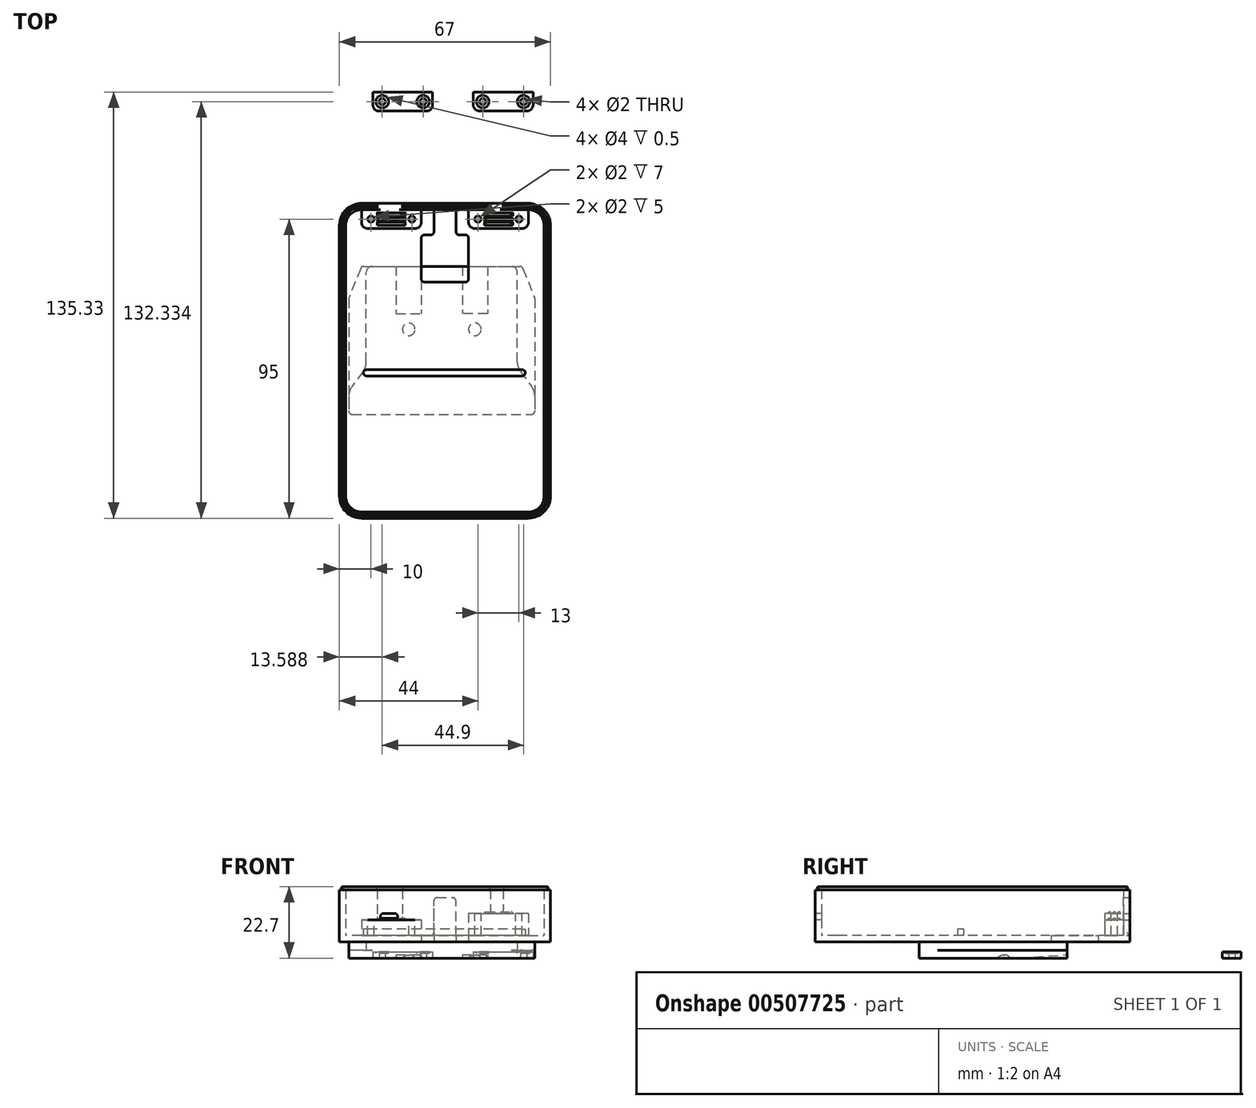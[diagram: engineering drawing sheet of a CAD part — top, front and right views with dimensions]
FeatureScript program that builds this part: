
annotation { "Feature Type Name" : "Feature", "Feature Type Description" : "" }
export const myFeature = defineFeature(function(context is Context, id is Id, definition is map)
    precondition{}
    {
        {
            var Q0;
            Q0=qCreatedBy(makeId("Top.planeOp"),FACE);
            var sketch = newSketch(context, id + "F0", { "sketchPlane" : qUnion([Q0])});
            skLineSegment(sketch, "E0.bottom", {"start": v(4, 0) * mm, "end": v(55, 0) * mm});
            skLineSegment(sketch, "E0.top", {"start": v(0, -47) * mm, "end": v(59, -47) * mm});
            skLineSegment(sketch, "E0.left", {"start": v(0, -10) * mm, "end": v(0, -47) * mm});
            skLineSegment(sketch, "E0.right", {"start": v(59, -10) * mm, "end": v(59, -47) * mm});
            skLineSegment(sketch, "E1", {"start": v(4, 0) * mm, "end": v(0, -10) * mm});
            skPoint(sketch, "E2.orphan", {"position": v(0, 0) * mm});
            skLineSegment(sketch, "E3", {"start": v(55, 0) * mm, "end": v(59, -10) * mm});
            skPoint(sketch, "E4.orphan", {"position": v(59, 0) * mm});
            skSolve(sketch);
        }
        {
            var Q0;
            Q0=makeQuery(id+"F0.imprint","IMPRINT",FACE,{"disambiguationData":[TD([[makeQuery(id+"F0.imprint","IMPRINT",EDGE,{"derivedFrom":sQuery(id+"F0.wireOp",EDGE,"E0.bottom")}),-1.0]])]});
            extrude(context, id + "F1", {"entities" : qUnion([Q0]), "depth" : 2.5 * mm, "offsetDistance" : 25 * mm});
        }
        {
            var Q0;
            Q0=makeQuery(id+"F1.opExtrude","CAP_FACE",FACE,{"disambiguationData":[OSD([sQuery(id+"F0.wireOp",EDGE,"E0.bottom"),sQuery(id+"F0.wireOp",EDGE,"E0.top"),sQuery(id+"F0.wireOp",EDGE,"E0.left"),sQuery(id+"F0.wireOp",EDGE,"E0.right"),sQuery(id+"F0.wireOp",EDGE,"E1"),sQuery(id+"F0.wireOp",EDGE,"E3")])],"isStart":false});
            var sketch = newSketch(context, id + "F2", { "sketchPlane" : qUnion([Q0])});
            skLineSegment(sketch, "E5.bottom", {"start": v(0, -47) * mm, "end": v(59, -47) * mm});
            skLineSegment(sketch, "E5.left", {"start": v(0, -47) * mm, "end": v(0, -39.5) * mm});
            skLineSegment(sketch, "E5.right", {"start": v(59, -47) * mm, "end": v(59, -39.5) * mm});
            skLineSegment(sketch, "E6.top", {"start": v(7.5, 0) * mm, "end": v(51.5, 0) * mm});
            skLineSegment(sketch, "E6.left", {"start": v(5.5, -32) * mm, "end": v(5.5, -2) * mm});
            skLineSegment(sketch, "E6.right", {"start": v(53.5, -32) * mm, "end": v(53.5, -2) * mm});
            skPoint(sketch, "E7.visualSharp", {"position": v(5.5, 0) * mm});
            skArc(sketch, "E7.filletArc", {"start": v(7.5, 0) * mm, "mid": v(6.09, -0.59) * mm, "end": v(5.5, -2) * mm});
            skPoint(sketch, "E8.visualSharp", {"position": v(53.5, 0) * mm});
            skArc(sketch, "E8.filletArc", {"start": v(53.5, -2) * mm, "mid": v(52.91, -0.59) * mm, "end": v(51.5, 0) * mm});
            skLineSegment(sketch, "E9", {"start": v(53.5, -32) * mm, "end": v(59, -39.5) * mm});
            skLineSegment(sketch, "E10", {"start": v(5.5, -32) * mm, "end": v(0, -39.5) * mm});
            skPoint(sketch, "E11.orphan", {"position": v(0, -32) * mm});
            skPoint(sketch, "E12.orphan", {"position": v(59, -32) * mm});
            skSolve(sketch);
        }
        {
            var Q0;
            Q0=makeQuery(id+"F2.imprint","IMPRINT",FACE,{"disambiguationData":[TD([[makeQuery(id+"F2.imprint","IMPRINT",EDGE,{"derivedFrom":sQuery(id+"F2.wireOp",EDGE,"E5.bottom")}),1.0]])]});
            extrude(context, id + "F3", {"entities" : qUnion([Q0]), "operationType" : NewBodyOperationType.ADD, "depth" : 2.7 * mm, "offsetDistance" : 25 * mm});
        }
        {
            var Q0;
            Q0=makeQuery(id+"F3.opExtrude","CAP_FACE",FACE,{"disambiguationData":[OSD([sQuery(id+"F2.wireOp",EDGE,"E5.bottom"),sQuery(id+"F2.wireOp",EDGE,"E5.left"),sQuery(id+"F2.wireOp",EDGE,"E5.right"),sQuery(id+"F2.wireOp",EDGE,"E6.top"),sQuery(id+"F2.wireOp",EDGE,"E6.left"),sQuery(id+"F2.wireOp",EDGE,"E6.right"),sQuery(id+"F2.wireOp",EDGE,"E7.filletArc"),sQuery(id+"F2.wireOp",EDGE,"E8.filletArc"),sQuery(id+"F2.wireOp",EDGE,"E9"),sQuery(id+"F2.wireOp",EDGE,"E10")])],"isStart":false});
            var sketch = newSketch(context, id + "F4", { "sketchPlane" : qUnion([Q0])});
            skLineSegment(sketch, "E13.bottom", {"start": v(57, -80) * mm, "end": v(4, -80) * mm});
            skLineSegment(sketch, "E13.top", {"start": v(57, 20) * mm, "end": v(35, 20) * mm});
            skLineSegment(sketch, "E13.left", {"start": v(64, -73) * mm, "end": v(64, 13) * mm});
            skLineSegment(sketch, "E13.right", {"start": v(-3, -73) * mm, "end": v(-3, 13) * mm});
            skPoint(sketch, "E14.visualSharp", {"position": v(-3, 20) * mm});
            skArc(sketch, "E14.filletArc", {"start": v(4, 20) * mm, "mid": v(-0.95, 17.95) * mm, "end": v(-3, 13) * mm});
            skPoint(sketch, "E15.visualSharp", {"position": v(64, 20) * mm});
            skArc(sketch, "E15.filletArc", {"start": v(64, 13) * mm, "mid": v(61.95, 17.95) * mm, "end": v(57, 20) * mm});
            skPoint(sketch, "E16.visualSharp", {"position": v(64, -80) * mm});
            skArc(sketch, "E16.filletArc", {"start": v(57, -80) * mm, "mid": v(61.95, -77.95) * mm, "end": v(64, -73) * mm});
            skPoint(sketch, "E17.visualSharp", {"position": v(-3, -80) * mm});
            skArc(sketch, "E17.filletArc", {"start": v(-3, -73) * mm, "mid": v(-0.95, -77.95) * mm, "end": v(4, -80) * mm});
            skLineSegment(sketch, "E18.top", {"start": v(27, -5) * mm, "end": v(34, -5) * mm});
            skLineSegment(sketch, "E18.left", {"start": v(27, 19) * mm, "end": v(27, 11) * mm});
            skLineSegment(sketch, "E18.right", {"start": v(34, 19) * mm, "end": v(34, 11) * mm});
            skLineSegment(sketch, "E19.filletArc", {"start": v(27, -5) * mm, "end": v(27, -5) * mm});
            skLineSegment(sketch, "E20.filletArc", {"start": v(34, -5) * mm, "end": v(34, -5) * mm});
            skLineSegment(sketch, "E21.trimOffspring", {"start": v(26, 20) * mm, "end": v(4, 20) * mm});
            skPoint(sketch, "E22.visualSharp", {"position": v(27, 20) * mm});
            skArc(sketch, "E22.filletArc", {"start": v(27, 19) * mm, "mid": v(26.7, 19.7) * mm, "end": v(26, 20) * mm});
            skPoint(sketch, "E23.visualSharp", {"position": v(34, 20) * mm});
            skArc(sketch, "E23.filletArc", {"start": v(35, 20) * mm, "mid": v(34.3, 19.7) * mm, "end": v(34, 19) * mm});
            skPoint(sketch, "E24", {"position": v(34, 10) * mm});
            skLineSegment(sketch, "E25", {"start": v(34, -5) * mm, "end": v(37, -5) * mm});
            skLineSegment(sketch, "E26", {"start": v(38, -4) * mm, "end": v(38, 9) * mm});
            skLineSegment(sketch, "E27", {"start": v(37, 10) * mm, "end": v(35, 10) * mm});
            skPoint(sketch, "E28", {"position": v(27, 10) * mm});
            skLineSegment(sketch, "E29", {"start": v(26, 10) * mm, "end": v(24, 10) * mm});
            skLineSegment(sketch, "E30", {"start": v(23, 9) * mm, "end": v(23, -4) * mm});
            skLineSegment(sketch, "E31", {"start": v(24, -5) * mm, "end": v(27, -5) * mm});
            skPoint(sketch, "E32.visualSharp", {"position": v(23, 10) * mm});
            skArc(sketch, "E32.filletArc", {"start": v(24, 10) * mm, "mid": v(23.3, 9.7) * mm, "end": v(23, 9) * mm});
            skPoint(sketch, "E33.visualSharp", {"position": v(23, -5) * mm});
            skArc(sketch, "E33.filletArc", {"start": v(23, -4) * mm, "mid": v(23.3, -4.7) * mm, "end": v(24, -5) * mm});
            skPoint(sketch, "E34.visualSharp", {"position": v(38, -5) * mm});
            skArc(sketch, "E34.filletArc", {"start": v(37, -5) * mm, "mid": v(37.7, -4.7) * mm, "end": v(38, -4) * mm});
            skPoint(sketch, "E35.visualSharp", {"position": v(38, 10) * mm});
            skArc(sketch, "E35.filletArc", {"start": v(38, 9) * mm, "mid": v(37.7, 9.7) * mm, "end": v(37, 10) * mm});
            skArc(sketch, "E36.filletArc", {"start": v(26, 10) * mm, "mid": v(26.7, 10.3) * mm, "end": v(27, 11) * mm});
            skArc(sketch, "E37.filletArc", {"start": v(34, 11) * mm, "mid": v(34.3, 10.3) * mm, "end": v(35, 10) * mm});
            skSolve(sketch);
        }
        {
            var Q0;
            Q0 = qSketchRegion(id + "F4", true);
            extrude(context, id + "F5", {"entities" : qUnion([Q0]), "operationType" : NewBodyOperationType.ADD, "depth" : 2 * mm, "offsetDistance" : 25 * mm});
        }
        {
            var Q0;
            Q0=makeQuery(id+"F5.opExtrude","CAP_FACE",FACE,{"disambiguationData":[OSD([sQuery(id+"F4.wireOp",EDGE,"E13.bottom"),sQuery(id+"F4.wireOp",EDGE,"E13.top"),sQuery(id+"F4.wireOp",EDGE,"E13.left"),sQuery(id+"F4.wireOp",EDGE,"E13.right"),sQuery(id+"F4.wireOp",EDGE,"E14.filletArc"),sQuery(id+"F4.wireOp",EDGE,"E15.filletArc"),sQuery(id+"F4.wireOp",EDGE,"E16.filletArc"),sQuery(id+"F4.wireOp",EDGE,"E17.filletArc"),sQuery(id+"F4.wireOp",EDGE,"E18.top"),sQuery(id+"F4.wireOp",EDGE,"E18.left"),sQuery(id+"F4.wireOp",EDGE,"E18.right"),sQuery(id+"F4.wireOp",EDGE,"E19.filletArc"),sQuery(id+"F4.wireOp",EDGE,"E20.filletArc"),sQuery(id+"F4.wireOp",EDGE,"E21.trimOffspring"),sQuery(id+"F4.wireOp",EDGE,"E22.filletArc"),sQuery(id+"F4.wireOp",EDGE,"E23.filletArc")])],"isStart":false});
            var sketch = newSketch(context, id + "F6", { "sketchPlane" : qUnion([Q0])});
            skLineSegment(sketch, "E38.bottom", {"start": v(57, 20) * mm, "end": v(4, 20) * mm});
            skLineSegment(sketch, "E38.top", {"start": v(57, -80) * mm, "end": v(4, -80) * mm});
            skLineSegment(sketch, "E38.left", {"start": v(64, 13) * mm, "end": v(64, -73) * mm});
            skLineSegment(sketch, "E38.right", {"start": v(-3, 13) * mm, "end": v(-3, -73) * mm});
            skPoint(sketch, "E39.visualSharp", {"position": v(-3, 20) * mm});
            skArc(sketch, "E39.filletArc", {"start": v(4, 20) * mm, "mid": v(-0.95, 17.95) * mm, "end": v(-3, 13) * mm});
            skPoint(sketch, "E40.visualSharp", {"position": v(64, 20) * mm});
            skArc(sketch, "E40.filletArc", {"start": v(64, 13) * mm, "mid": v(61.95, 17.95) * mm, "end": v(57, 20) * mm});
            skPoint(sketch, "E41.visualSharp", {"position": v(64, -80) * mm});
            skArc(sketch, "E41.filletArc", {"start": v(57, -80) * mm, "mid": v(61.95, -77.95) * mm, "end": v(64, -73) * mm});
            skPoint(sketch, "E42.visualSharp", {"position": v(-3, -80) * mm});
            skArc(sketch, "E42.filletArc", {"start": v(-3, -73) * mm, "mid": v(-0.95, -77.95) * mm, "end": v(4, -80) * mm});
            skArc(sketch, "E43.0", {"start": v(62, 13) * mm, "mid": v(60.54, 16.54) * mm, "end": v(57, 18) * mm});
            skLineSegment(sketch, "E43.1", {"start": v(62, 13) * mm, "end": v(62, -73) * mm});
            skLineSegment(sketch, "E43.2", {"start": v(57, 18) * mm, "end": v(4, 18) * mm});
            skArc(sketch, "E43.3", {"start": v(57, -78) * mm, "mid": v(60.54, -76.54) * mm, "end": v(62, -73) * mm});
            skArc(sketch, "E43.4", {"start": v(4, 18) * mm, "mid": v(0.46, 16.54) * mm, "end": v(-1, 13) * mm});
            skLineSegment(sketch, "E43.5", {"start": v(-1, 13) * mm, "end": v(-1, -73) * mm});
            skArc(sketch, "E43.6", {"start": v(-1, -73) * mm, "mid": v(0.46, -76.54) * mm, "end": v(4, -78) * mm});
            skLineSegment(sketch, "E43.7", {"start": v(57, -78) * mm, "end": v(4, -78) * mm});
            skSolve(sketch);
        }
        {
            var Q0;
            Q0 = qSketchRegion(id + "F6", true);
            extrude(context, id + "F7", {"entities" : qUnion([Q0]), "operationType" : NewBodyOperationType.ADD, "depth" : 14.5 * mm, "offsetDistance" : 25 * mm});
        }
        {
            var Q0;
            Q0=makeQuery(id+"F7.boolean.opBoolean","MERGE",FACE,{"derivedFrom":[makeQuery(id+"F5.opExtrude","SWEPT_FACE",FACE,{"disambiguationData":[OSD([sQuery(id+"F4.wireOp",EDGE,"E13.top")])]}),makeQuery(id+"F5.opExtrude","SWEPT_FACE",FACE,{"disambiguationData":[OSD([sQuery(id+"F4.wireOp",EDGE,"E21.trimOffspring")])]}),makeQuery(id+"F7.opExtrude","SWEPT_FACE",FACE,{"disambiguationData":[OSD([sQuery(id+"F6.wireOp",EDGE,"E38.bottom")])]})]});
            var sketch = newSketch(context, id + "F8", { "sketchPlane" : qUnion([Q0])});
            skLineSegment(sketch, "E44.bottom", {"start": v(-27, 7.2) * mm, "end": v(-34, 7.2) * mm});
            skLineSegment(sketch, "E44.top", {"start": v(-28, 19.2) * mm, "end": v(-33, 19.2) * mm});
            skLineSegment(sketch, "E44.left", {"start": v(-27, 7.2) * mm, "end": v(-27, 18.2) * mm});
            skLineSegment(sketch, "E44.right", {"start": v(-34, 7.2) * mm, "end": v(-34, 18.2) * mm});
            skPoint(sketch, "E45.visualSharp", {"position": v(-34, 19.2) * mm});
            skArc(sketch, "E45.filletArc", {"start": v(-33, 19.2) * mm, "mid": v(-33.7, 18.9) * mm, "end": v(-34, 18.2) * mm});
            skPoint(sketch, "E46.visualSharp", {"position": v(-27, 19.2) * mm});
            skArc(sketch, "E46.filletArc", {"start": v(-27, 18.2) * mm, "mid": v(-27.3, 18.9) * mm, "end": v(-28, 19.2) * mm});
            skLineSegment(sketch, "E47.bottom", {"start": v(-49, 21.7) * mm, "end": v(-45, 21.7) * mm});
            skLineSegment(sketch, "E47.top", {"start": v(-48, 14.2) * mm, "end": v(-46, 14.2) * mm});
            skLineSegment(sketch, "E47.left", {"start": v(-49, 21.7) * mm, "end": v(-49, 15.2) * mm});
            skLineSegment(sketch, "E47.right", {"start": v(-45, 21.7) * mm, "end": v(-45, 15.2) * mm});
            skPoint(sketch, "E48.visualSharp", {"position": v(-49, 14.2) * mm});
            skArc(sketch, "E48.filletArc", {"start": v(-49, 15.2) * mm, "mid": v(-48.7, 14.5) * mm, "end": v(-48, 14.2) * mm});
            skPoint(sketch, "E49.visualSharp", {"position": v(-45, 14.2) * mm});
            skArc(sketch, "E49.filletArc", {"start": v(-46, 14.2) * mm, "mid": v(-45.3, 14.5) * mm, "end": v(-45, 15.2) * mm});
            skLineSegment(sketch, "E50.bottom", {"start": v(-9, 21.7) * mm, "end": v(-17, 21.7) * mm});
            skLineSegment(sketch, "E50.top", {"start": v(-10, 12.2) * mm, "end": v(-16, 12.2) * mm});
            skLineSegment(sketch, "E50.left", {"start": v(-9, 21.7) * mm, "end": v(-9, 13.2) * mm});
            skLineSegment(sketch, "E50.right", {"start": v(-17, 21.7) * mm, "end": v(-17, 13.2) * mm});
            skPoint(sketch, "E51.visualSharp", {"position": v(-17, 12.2) * mm});
            skArc(sketch, "E51.filletArc", {"start": v(-17, 13.2) * mm, "mid": v(-16.7, 12.5) * mm, "end": v(-16, 12.2) * mm});
            skPoint(sketch, "E52.visualSharp", {"position": v(-9, 12.2) * mm});
            skArc(sketch, "E52.filletArc", {"start": v(-10, 12.2) * mm, "mid": v(-9.3, 12.5) * mm, "end": v(-9, 13.2) * mm});
            skSolve(sketch);
        }
        {
            var Q0;
            Q0=makeQuery(id+"FvWDrRj3cYPkLqx_1.boolean.opBoolean","MERGE",FACE,{"derivedFrom":[makeQuery(id+"F5.opExtrude","CAP_FACE",FACE,{"disambiguationData":[OSD([sQuery(id+"F4.wireOp",EDGE,"E13.bottom"),sQuery(id+"F4.wireOp",EDGE,"E13.top"),sQuery(id+"F4.wireOp",EDGE,"E13.left"),sQuery(id+"F4.wireOp",EDGE,"E13.right"),sQuery(id+"F4.wireOp",EDGE,"E14.filletArc"),sQuery(id+"F4.wireOp",EDGE,"E15.filletArc"),sQuery(id+"F4.wireOp",EDGE,"E16.filletArc"),sQuery(id+"F4.wireOp",EDGE,"E17.filletArc"),sQuery(id+"F4.wireOp",EDGE,"E18.top"),sQuery(id+"F4.wireOp",EDGE,"E18.left"),sQuery(id+"F4.wireOp",EDGE,"E18.right"),sQuery(id+"F4.wireOp",EDGE,"E19.filletArc"),sQuery(id+"F4.wireOp",EDGE,"E20.filletArc"),sQuery(id+"F4.wireOp",EDGE,"E21.trimOffspring"),sQuery(id+"F4.wireOp",EDGE,"E22.filletArc"),sQuery(id+"F4.wireOp",EDGE,"E23.filletArc")])],"isStart":false}),makeQuery(id+"FvWDrRj3cYPkLqx_1.opExtrude","SWEPT_FACE",FACE,{"disambiguationData":[OSD([sQuery(id+"F8.wireOp",EDGE,"E44.bottom")])]})]});
            var sketch = newSketch(context, id + "F9", { "sketchPlane" : qUnion([Q0])});
            skLineSegment(sketch, "E53.bottom", {"start": v(54.99, -34.8) * mm, "end": v(5.63, -34.8) * mm});
            skLineSegment(sketch, "E53.top", {"start": v(54.99, -32.8) * mm, "end": v(5.63, -32.8) * mm});
            skLineSegment(sketch, "E53.left", {"start": v(55.99, -33.8) * mm, "end": v(55.99, -33.8) * mm});
            skLineSegment(sketch, "E53.right", {"start": v(4.63, -33.8) * mm, "end": v(4.63, -33.8) * mm});
            skPoint(sketch, "E54.visualSharp", {"position": v(4.63, -32.8) * mm});
            skArc(sketch, "E54.filletArc", {"start": v(5.63, -32.8) * mm, "mid": v(4.92, -33.1) * mm, "end": v(4.63, -33.8) * mm});
            skPoint(sketch, "E55.visualSharp", {"position": v(4.63, -34.8) * mm});
            skArc(sketch, "E55.filletArc", {"start": v(4.63, -33.8) * mm, "mid": v(4.92, -34.5) * mm, "end": v(5.63, -34.8) * mm});
            skPoint(sketch, "E56.visualSharp", {"position": v(55.99, -32.8) * mm});
            skArc(sketch, "E56.filletArc", {"start": v(55.99, -33.8) * mm, "mid": v(55.7, -33.1) * mm, "end": v(54.99, -32.8) * mm});
            skPoint(sketch, "E57.visualSharp", {"position": v(55.99, -34.8) * mm});
            skArc(sketch, "E57.filletArc", {"start": v(54.99, -34.8) * mm, "mid": v(55.7, -34.5) * mm, "end": v(55.99, -33.8) * mm});
            skSolve(sketch);
        }
        {
            var Q0;
            Q0 = qSketchRegion(id + "F9", true);
            var Q1;
            Q1 = qSketchRegion(id + "F11", true);
            extrude(context, id + "F10", {"entities" : qUnion([Q0, Q1]), "operationType" : NewBodyOperationType.ADD, "depth" : 2 * mm});
        }
        {
            var Q0;
            Q0=makeQuery(id+"FvWDrRj3cYPkLqx_1.boolean.opBoolean","MERGE",FACE,{"derivedFrom":[makeQuery(id+"F5.opExtrude","CAP_FACE",FACE,{"disambiguationData":[OSD([sQuery(id+"F4.wireOp",EDGE,"E13.bottom"),sQuery(id+"F4.wireOp",EDGE,"E13.top"),sQuery(id+"F4.wireOp",EDGE,"E13.left"),sQuery(id+"F4.wireOp",EDGE,"E13.right"),sQuery(id+"F4.wireOp",EDGE,"E14.filletArc"),sQuery(id+"F4.wireOp",EDGE,"E15.filletArc"),sQuery(id+"F4.wireOp",EDGE,"E16.filletArc"),sQuery(id+"F4.wireOp",EDGE,"E17.filletArc"),sQuery(id+"F4.wireOp",EDGE,"E18.top"),sQuery(id+"F4.wireOp",EDGE,"E18.left"),sQuery(id+"F4.wireOp",EDGE,"E18.right"),sQuery(id+"F4.wireOp",EDGE,"E19.filletArc"),sQuery(id+"F4.wireOp",EDGE,"E20.filletArc"),sQuery(id+"F4.wireOp",EDGE,"E21.trimOffspring"),sQuery(id+"F4.wireOp",EDGE,"E22.filletArc"),sQuery(id+"F4.wireOp",EDGE,"E23.filletArc")])],"isStart":false}),makeQuery(id+"FvWDrRj3cYPkLqx_1.opExtrude","SWEPT_FACE",FACE,{"disambiguationData":[OSD([sQuery(id+"F8.wireOp",EDGE,"E44.bottom")])]})]});
            var sketch = newSketch(context, id + "F11", { "sketchPlane" : qUnion([Q0])});
            skSolve(sketch);
        }
        {
            var Q0;
            Q0=makeQuery(id+"F8.imprint","IMPRINT",FACE,{"disambiguationData":[TD([[makeQuery(id+"F8.imprint","IMPRINT",EDGE,{"derivedFrom":sQuery(id+"F8.wireOp",EDGE,"E47.bottom")}),-1.0]])]});
            var Q1;
            Q1=makeQuery(id+"F8.imprint","IMPRINT",FACE,{"disambiguationData":[TD([[makeQuery(id+"F8.imprint","IMPRINT",EDGE,{"derivedFrom":sQuery(id+"F8.wireOp",EDGE,"E44.top")}),1.0]])]});
            var Q2;
            Q2=makeQuery(id+"F8.imprint","IMPRINT",FACE,{"disambiguationData":[TD([[makeQuery(id+"F8.imprint","IMPRINT",EDGE,{"derivedFrom":sQuery(id+"F8.wireOp",EDGE,"E50.bottom")}),-1.0]])]});
            extrude(context, id + "F12", {"entities" : qUnion([Q0, Q1, Q2]), "operationType" : NewBodyOperationType.REMOVE, "oppositeDirection" : true, "depth" : 2 * mm});
        }
        {
            var Q0;
            Q0=makeQuery(id+"F7.boolean.opBoolean","MERGE",FACE,{"derivedFrom":[makeQuery(id+"F5.opExtrude","SWEPT_FACE",FACE,{"disambiguationData":[OSD([sQuery(id+"F4.wireOp",EDGE,"E13.bottom")])]}),makeQuery(id+"F7.opExtrude","SWEPT_FACE",FACE,{"disambiguationData":[OSD([sQuery(id+"F6.wireOp",EDGE,"E38.top")])]})]});
            var sketch = newSketch(context, id + "F13", { "sketchPlane" : qUnion([Q0])});
            skLineSegment(sketch, "E58.bottom", {"start": v(11, 14.2) * mm, "end": v(14.5, 14.2) * mm});
            skLineSegment(sketch, "E58.top", {"start": v(11, 12.2) * mm, "end": v(14.5, 12.2) * mm});
            skLineSegment(sketch, "E58.left", {"start": v(10, 13.2) * mm, "end": v(10, 13.2) * mm});
            skLineSegment(sketch, "E58.right", {"start": v(15.5, 13.2) * mm, "end": v(15.5, 13.2) * mm});
            skPoint(sketch, "E59.visualSharp", {"position": v(10, 14.2) * mm});
            skArc(sketch, "E59.filletArc", {"start": v(11, 14.2) * mm, "mid": v(10.3, 13.9) * mm, "end": v(10, 13.2) * mm});
            skPoint(sketch, "E60.visualSharp", {"position": v(10, 12.2) * mm});
            skArc(sketch, "E60.filletArc", {"start": v(10, 13.2) * mm, "mid": v(10.3, 12.5) * mm, "end": v(11, 12.2) * mm});
            skPoint(sketch, "E61.visualSharp", {"position": v(15.5, 14.2) * mm});
            skArc(sketch, "E61.filletArc", {"start": v(15.5, 13.2) * mm, "mid": v(15.2, 13.9) * mm, "end": v(14.5, 14.2) * mm});
            skPoint(sketch, "E62.visualSharp", {"position": v(15.5, 12.2) * mm});
            skArc(sketch, "E62.filletArc", {"start": v(14.5, 12.2) * mm, "mid": v(15.2, 12.5) * mm, "end": v(15.5, 13.2) * mm});
            skSolve(sketch);
        }
        {
            var Q0;
            Q0=makeQuery(id+"F13.imprint","IMPRINT",FACE,{"disambiguationData":[TD([[makeQuery(id+"F13.imprint","IMPRINT",EDGE,{"derivedFrom":sQuery(id+"F13.wireOp",EDGE,"E58.bottom")}),-1.0]])]});
            extrude(context, id + "F14", {"entities" : qUnion([Q0]), "operationType" : NewBodyOperationType.REMOVE, "oppositeDirection" : true, "depth" : 2 * mm, "offsetDistance" : 25 * mm});
        }
        {
            var Q0;
            Q0=makeQuery(id+"F3.boolean.opBoolean","MERGE",EDGE,{"derivedFrom":[makeQuery(id+"F1.opExtrude","SWEPT_EDGE",EDGE,{"disambiguationData":[OSD([sQuery(id+"F0.wireOp",EDGE,"E0.top"),sQuery(id+"F0.wireOp",EDGE,"E0.left")])]}),makeQuery(id+"F3.opExtrude","SWEPT_EDGE",EDGE,{"disambiguationData":[OSD([sQuery(id+"F2.wireOp",EDGE,"E5.bottom"),sQuery(id+"F2.wireOp",EDGE,"E5.left")])]})]});
            var Q1;
            Q1=makeQuery(id+"F3.boolean.opBoolean","MERGE",EDGE,{"derivedFrom":[makeQuery(id+"F1.opExtrude","SWEPT_EDGE",EDGE,{"disambiguationData":[OSD([sQuery(id+"F0.wireOp",EDGE,"E0.top"),sQuery(id+"F0.wireOp",EDGE,"E0.right")])]}),makeQuery(id+"F3.opExtrude","SWEPT_EDGE",EDGE,{"disambiguationData":[OSD([sQuery(id+"F2.wireOp",EDGE,"E5.bottom"),sQuery(id+"F2.wireOp",EDGE,"E5.right")])]})]});
            var Q2;
            Q2=makeQuery(id+"F1.opExtrude","SWEPT_EDGE",EDGE,{"disambiguationData":[OSD([sQuery(id+"F0.wireOp",EDGE,"E0.bottom"),sQuery(id+"F0.wireOp",EDGE,"E1")])]});
            var Q3;
            Q3=makeQuery(id+"F1.opExtrude","SWEPT_EDGE",EDGE,{"disambiguationData":[OSD([sQuery(id+"F0.wireOp",EDGE,"E0.bottom"),sQuery(id+"F0.wireOp",EDGE,"E3")])]});
            var Q4;
            Q4=makeQuery(id+"F1.opExtrude","SWEPT_EDGE",EDGE,{"disambiguationData":[OSD([sQuery(id+"F0.wireOp",EDGE,"E0.right"),sQuery(id+"F0.wireOp",EDGE,"E3")])]});
            var Q5;
            Q5=makeQuery(id+"F1.opExtrude","SWEPT_EDGE",EDGE,{"disambiguationData":[OSD([sQuery(id+"F0.wireOp",EDGE,"E0.left"),sQuery(id+"F0.wireOp",EDGE,"E1")])]});
            fillet(context, id + "F15", {"entities" : qUnion([Q0, Q1, Q2, Q3, Q4, Q5]), "radius" : 1 * mm, "tangentPropagation" : true, "allowEdgeOverflow" : false});
        }
        {
            var Q0;
            Q0=makeQuery(id+"F3.opExtrude","SWEPT_EDGE",EDGE,{"disambiguationData":[OSD([sQuery(id+"F0.wireOp",EDGE,"E0.left"),sQuery(id+"F2.wireOp",EDGE,"E5.left"),sQuery(id+"F2.wireOp",EDGE,"E10")])]});
            var Q1;
            Q1=makeQuery(id+"F3.opExtrude","SWEPT_EDGE",EDGE,{"disambiguationData":[OSD([sQuery(id+"F0.wireOp",EDGE,"E0.right"),sQuery(id+"F2.wireOp",EDGE,"E5.right"),sQuery(id+"F2.wireOp",EDGE,"E9")])]});
            var Q2;
            Q2=makeQuery(id+"F3.opExtrude","SWEPT_EDGE",EDGE,{"disambiguationData":[OSD([sQuery(id+"F2.wireOp",EDGE,"E6.right"),sQuery(id+"F2.wireOp",EDGE,"E9")])]});
            var Q3;
            Q3=makeQuery(id+"F3.opExtrude","SWEPT_EDGE",EDGE,{"disambiguationData":[OSD([sQuery(id+"F2.wireOp",EDGE,"E6.left"),sQuery(id+"F2.wireOp",EDGE,"E10")])]});
            fillet(context, id + "F16", {"entities" : qUnion([Q0, Q1, Q2, Q3]), "radius" : 5 * mm, "tangentPropagation" : true, "allowEdgeOverflow" : false});
        }
        {
            var Q0;
            Q0=makeQuery(id+"F1.opExtrude","CAP_FACE",FACE,{"disambiguationData":[OSD([sQuery(id+"F0.wireOp",EDGE,"E0.bottom"),sQuery(id+"F0.wireOp",EDGE,"E0.top"),sQuery(id+"F0.wireOp",EDGE,"E0.left"),sQuery(id+"F0.wireOp",EDGE,"E0.right"),sQuery(id+"F0.wireOp",EDGE,"E1"),sQuery(id+"F0.wireOp",EDGE,"E3")])],"isStart":true});
            var sketch = newSketch(context, id + "F17", { "sketchPlane" : qUnion([Q0])});
            skLineSegment(sketch, "E63.bottom", {"start": v(15, 0) * mm, "end": v(23, 0) * mm});
            skLineSegment(sketch, "E63.top", {"start": v(15, 15) * mm, "end": v(23, 15) * mm});
            skLineSegment(sketch, "E63.left", {"start": v(15, 0) * mm, "end": v(15, 15) * mm});
            skLineSegment(sketch, "E63.right", {"start": v(23, 0) * mm, "end": v(23, 15) * mm});
            skLineSegment(sketch, "E64.bottom", {"start": v(44, 0) * mm, "end": v(36, 0) * mm});
            skLineSegment(sketch, "E64.top", {"start": v(44, 15) * mm, "end": v(36, 15) * mm});
            skLineSegment(sketch, "E64.left", {"start": v(44, 0) * mm, "end": v(44, 15) * mm});
            skLineSegment(sketch, "E64.right", {"start": v(36, 0) * mm, "end": v(36, 15) * mm});
            skSolve(sketch);
        }
        {
            var Q0;
            Q0=makeQuery(id+"F1.opExtrude","CAP_FACE",FACE,{"disambiguationData":[OSD([sQuery(id+"F0.wireOp",EDGE,"E0.bottom"),sQuery(id+"F0.wireOp",EDGE,"E0.top"),sQuery(id+"F0.wireOp",EDGE,"E0.left"),sQuery(id+"F0.wireOp",EDGE,"E0.right"),sQuery(id+"F0.wireOp",EDGE,"E1"),sQuery(id+"F0.wireOp",EDGE,"E3")])],"isStart":true});
            var sketch = newSketch(context, id + "F18", { "sketchPlane" : qUnion([Q0])});
            skCircle(sketch, "E65", {"center": v(19, 20) * mm, "radius": 2 * mm});
            skCircle(sketch, "E66", {"center": v(40, 20) * mm, "radius": 2 * mm});
            skSolve(sketch);
        }
        {
            var Q0;
            Q0 = qSketchRegion(id + "F18", true);
            extrude(context, id + "F19", {"entities" : qUnion([Q0]), "operationType" : NewBodyOperationType.REMOVE, "oppositeDirection" : true, "depth" : 1 * mm});
        }
        {
            var Q0;
            Q0=makeQuery(id+"F17.imprint","IMPRINT",FACE,{"disambiguationData":[TD([[makeQuery(id+"F17.imprint","IMPRINT",EDGE,{"derivedFrom":sQuery(id+"F17.wireOp",EDGE,"E64.bottom")}),1.0]])]});
            var Q1;
            Q1=makeQuery(id+"F17.imprint","IMPRINT",FACE,{"disambiguationData":[TD([[makeQuery(id+"F17.imprint","IMPRINT",EDGE,{"derivedFrom":sQuery(id+"F17.wireOp",EDGE,"E63.bottom")}),1.0]])]});
            extrude(context, id + "F20", {"entities" : qUnion([Q0, Q1]), "operationType" : NewBodyOperationType.REMOVE, "oppositeDirection" : true, "depth" : 1.1 * mm});
        }
        {
            var Q0;
            Q0=makeQuery(id+"F20.boolean.opBoolean","COPY",EDGE,{"derivedFrom":makeQuery(id+"F20.opExtrude","CAP_EDGE",EDGE,{"disambiguationData":[OSD([sQuery(id+"F17.wireOp",EDGE,"E63.top")])],"isStart":false})});
            chamfer(context, id + "F21", {"entities" : qUnion([Q0]), "chamferType" : ChamferType.TWO_OFFSETS, "width1" : 1.1 * mm, "oppositeDirection" : false, "width2" : 15 * mm, "tangentPropagation" : true});
        }
        {
            var Q0;
            Q0=makeQuery(id+"F20.boolean.opBoolean","COPY",EDGE,{"derivedFrom":makeQuery(id+"F20.opExtrude","CAP_EDGE",EDGE,{"disambiguationData":[OSD([sQuery(id+"F17.wireOp",EDGE,"E64.top")])],"isStart":false})});
            chamfer(context, id + "F22", {"entities" : qUnion([Q0]), "chamferType" : ChamferType.TWO_OFFSETS, "width1" : 15 * mm, "oppositeDirection" : false, "width2" : 1.1 * mm, "tangentPropagation" : true});
        }
        {
            var Q0;
            Q0=makeQuery(id+"F19.boolean.opBoolean","COPY",EDGE,{"derivedFrom":makeQuery(id+"F19.opExtrude","CAP_EDGE",EDGE,{"disambiguationData":[OSD([sQuery(id+"F18.wireOp",EDGE,"E66")])],"isStart":false})});
            var Q1;
            Q1=makeQuery(id+"F19.boolean.opBoolean","COPY",EDGE,{"derivedFrom":makeQuery(id+"F19.opExtrude","CAP_EDGE",EDGE,{"disambiguationData":[OSD([sQuery(id+"F18.wireOp",EDGE,"E65")])],"isStart":false})});
            fillet(context, id + "F23", {"entities" : qUnion([Q0, Q1]), "radius" : 2 * mm, "tangentPropagation" : true, "allowEdgeOverflow" : false});
        }
        {
            var Q0;
            {var subQ0=sQuery(id+"F6.wireOp",EDGE,"E43.2");var subQ1=sQuery(id+"F6.wireOp",EDGE,"E43.1");var subQ2=sQuery(id+"F6.wireOp",EDGE,"E42.filletArc");var subQ3=sQuery(id+"F6.wireOp",EDGE,"E41.filletArc");var subQ4=sQuery(id+"F6.wireOp",EDGE,"E40.filletArc");var subQ5=sQuery(id+"F6.wireOp",EDGE,"E39.filletArc");var subQ6=sQuery(id+"F6.wireOp",EDGE,"E38.right");var subQ7=sQuery(id+"F6.wireOp",EDGE,"E38.left");var subQ8=sQuery(id+"F6.wireOp",EDGE,"E38.top");var subQ9=sQuery(id+"F6.wireOp",EDGE,"E43.4");var subQ10=sQuery(id+"F6.wireOp",EDGE,"E43.3");var subQ11=sQuery(id+"F6.wireOp",EDGE,"E38.bottom");var subQ12=sQuery(id+"F6.wireOp",EDGE,"E43.0");var subQ13=sQuery(id+"F6.wireOp",EDGE,"E43.5");var subQ14=sQuery(id+"F6.wireOp",EDGE,"E43.6");var subQ15=sQuery(id+"F6.wireOp",EDGE,"E43.7");Q0=makeQuery(id+"F12.boolean.opBoolean","SPLIT",FACE,{"disambiguationData":[TD([makeQuery(id+"F5.opExtrude","SWEPT_FACE",FACE,{"disambiguationData":[OSD([sQuery(id+"F4.wireOp",EDGE,"E13.bottom")])]})])],"derivedFrom":makeQuery(id+"F7.opExtrude","CAP_FACE",FACE,{"disambiguationData":[OSD([subQ11,subQ8,subQ7,subQ6,subQ5,subQ4,subQ3,subQ2,subQ12,subQ1,subQ0,subQ10,subQ9,subQ13,subQ14,subQ15])],"isStart":false})});}
            var sketch = newSketch(context, id + "F24", { "sketchPlane" : qUnion([Q0])});
            skLineSegment(sketch, "E67.0", {"start": v(57, 19.25) * mm, "end": v(49, 19.25) * mm});
            skArc(sketch, "E67.1", {"start": v(63.25, 13) * mm, "mid": v(61.42, 17.42) * mm, "end": v(57, 19.25) * mm});
            skLineSegment(sketch, "E67.2", {"start": v(63.25, -73) * mm, "end": v(63.25, 13) * mm});
            skArc(sketch, "E67.3", {"start": v(57, -79.25) * mm, "mid": v(61.42, -77.42) * mm, "end": v(63.25, -73) * mm});
            skLineSegment(sketch, "E67.4", {"start": v(57, -79.25) * mm, "end": v(4, -79.25) * mm});
            skLineSegment(sketch, "E67.5", {"start": v(9, 19.25) * mm, "end": v(4, 19.25) * mm});
            skArc(sketch, "E67.6", {"start": v(4, 19.25) * mm, "mid": v(-0.42, 17.42) * mm, "end": v(-2.25, 13) * mm});
            skLineSegment(sketch, "E67.7", {"start": v(-2.25, -73) * mm, "end": v(-2.25, 13) * mm});
            skArc(sketch, "E67.8", {"start": v(-2.25, -73) * mm, "mid": v(-0.42, -77.42) * mm, "end": v(4, -79.25) * mm});
            skLineSegment(sketch, "E68.0", {"start": v(57, 18.75) * mm, "end": v(49, 18.75) * mm});
            skArc(sketch, "E68.1", {"start": v(62.75, 13) * mm, "mid": v(61.07, 17.07) * mm, "end": v(57, 18.75) * mm});
            skLineSegment(sketch, "E68.2", {"start": v(62.75, 13) * mm, "end": v(62.75, -73) * mm});
            skArc(sketch, "E68.3", {"start": v(57, -78.75) * mm, "mid": v(61.07, -77.07) * mm, "end": v(62.75, -73) * mm});
            skLineSegment(sketch, "E68.4", {"start": v(57, -78.75) * mm, "end": v(4, -78.75) * mm});
            skLineSegment(sketch, "E68.5", {"start": v(9, 18.75) * mm, "end": v(4, 18.75) * mm});
            skArc(sketch, "E68.6", {"start": v(4, 18.75) * mm, "mid": v(-0.07, 17.07) * mm, "end": v(-1.75, 13) * mm});
            skLineSegment(sketch, "E68.7", {"start": v(-1.75, 13) * mm, "end": v(-1.75, -73) * mm});
            skArc(sketch, "E68.8", {"start": v(-1.75, -73) * mm, "mid": v(-0.07, -77.07) * mm, "end": v(4, -78.75) * mm});
            skLineSegment(sketch, "E69.0", {"start": v(45, 19.25) * mm, "end": v(17, 19.25) * mm});
            skLineSegment(sketch, "E70.0", {"start": v(45, 18.75) * mm, "end": v(17, 18.75) * mm});
            skLineSegment(sketch, "E71", {"start": v(17, 19.25) * mm, "end": v(17, 18.75) * mm});
            skLineSegment(sketch, "E72", {"start": v(45, 19.25) * mm, "end": v(45, 18.75) * mm});
            skSolve(sketch);
        }
        {
            var Q0;
            {var subQ2=sQuery(id+"F24.wireOp",EDGE,"E67.0");Q0=makeQuery(id+"F24.imprint","IMPRINT",FACE,{"disambiguationData":[TD([[makeQuery(id+"F24.imprint","IMPRINT",EDGE,{"derivedFrom":subQ2}),1.0]])]});}
            extrude(context, id + "F25", {"entities" : qUnion([Q0]), "operationType" : NewBodyOperationType.ADD, "depth" : 1 * mm, "offsetDistance" : 25 * mm});
        }
        {
            var Q0;
            Q0 = qSketchRegion(id + "F24", true);
            extrude(context, id + "F26", {"entities" : qUnion([Q0]), "operationType" : NewBodyOperationType.ADD, "depth" : 1 * mm, "offsetDistance" : 25 * mm});
        }
        {
            var Q0;
            Q0=makeQuery(id+"F25.opExtrude","CAP_EDGE",EDGE,{"disambiguationData":[OSD([sQuery(id+"F6.wireOp",EDGE,"E38.bottom"),sQuery(id+"F8.wireOp",EDGE,"E47.bottom"),sQuery(id+"F8.wireOp",EDGE,"E47.left")])],"isStart":false});
            var Q1;
            Q1=makeQuery(id+"F26.opExtrude","CAP_EDGE",EDGE,{"disambiguationData":[OSD([sQuery(id+"F24.wireOp",EDGE,"E72")])],"isStart":false});
            var Q2;
            Q2=makeQuery(id+"F26.opExtrude","CAP_EDGE",EDGE,{"disambiguationData":[OSD([sQuery(id+"F24.wireOp",EDGE,"E71")])],"isStart":false});
            var Q3;
            Q3=makeQuery(id+"F25.opExtrude","CAP_EDGE",EDGE,{"disambiguationData":[OSD([sQuery(id+"F6.wireOp",EDGE,"E38.bottom"),sQuery(id+"F8.wireOp",EDGE,"E50.bottom"),sQuery(id+"F8.wireOp",EDGE,"E50.left")])],"isStart":false});
            var Q4;
            Q4=makeQuery(id+"F12.boolean.opBoolean","COPY",EDGE,{"derivedFrom":makeQuery(id+"F12.opExtrude","SWEPT_EDGE",EDGE,{"disambiguationData":[OSD([sQuery(id+"F8.wireOp",EDGE,"E44.bottom"),sQuery(id+"F8.wireOp",EDGE,"E44.right")])]})});
            var Q5;
            Q5=makeQuery(id+"F12.boolean.opBoolean","COPY",EDGE,{"derivedFrom":makeQuery(id+"F12.opExtrude","SWEPT_EDGE",EDGE,{"disambiguationData":[OSD([sQuery(id+"F8.wireOp",EDGE,"E44.bottom"),sQuery(id+"F8.wireOp",EDGE,"E44.left")])]})});
            fillet(context, id + "F27", {"entities" : qUnion([Q0, Q1, Q2, Q3, Q4, Q5]), "radius" : 1 * mm, "tangentPropagation" : true, "allowEdgeOverflow" : false});
        }
        {
            var Q0;
            {var subQ6=sQuery(id+"F4.wireOp",EDGE,"E18.top");Q0=makeQuery(id+"F11.imprint","IMPRINT",FACE,{"disambiguationData":[TD([[makeQuery(id+"F11.imprint","IMPRINT",EDGE,{"derivedFrom":makeQuery(id+"F5.opExtrude","CAP_EDGE",EDGE,{"disambiguationData":[OSD([subQ6])],"isStart":false})}),-1.0]])]});}
            var sketch = newSketch(context, id + "F28", { "sketchPlane" : qUnion([Q0])});
            skLineSegment(sketch, "E73.bottom", {"start": v(38, 12) * mm, "end": v(57, 12) * mm});
            skLineSegment(sketch, "E73.top", {"start": v(38, 18) * mm, "end": v(57, 18) * mm});
            skLineSegment(sketch, "E73.left", {"start": v(38, 12) * mm, "end": v(38, 18) * mm});
            skLineSegment(sketch, "E73.right", {"start": v(57, 12) * mm, "end": v(57, 18) * mm});
            skSolve(sketch);
        }
        {
            var Q0;
            Q0 = qSketchRegion(id + "F28", true);
            extrude(context, id + "F29", {"entities" : qUnion([Q0]), "operationType" : NewBodyOperationType.ADD, "depth" : 7 * mm, "offsetDistance" : 25 * mm});
        }
        {
            var Q0;
            Q0=makeQuery(id+"F29.opExtrude","SWEPT_EDGE",EDGE,{"disambiguationData":[OSD([sQuery(id+"F28.wireOp",EDGE,"E73.bottom"),sQuery(id+"F28.wireOp",EDGE,"E73.left")])]});
            var Q1;
            Q1=makeQuery(id+"F29.opExtrude","SWEPT_EDGE",EDGE,{"disambiguationData":[OSD([sQuery(id+"F28.wireOp",EDGE,"E73.bottom"),sQuery(id+"F28.wireOp",EDGE,"E73.right")])]});
            fillet(context, id + "F30", {"entities" : qUnion([Q0, Q1]), "radius" : 2 * mm, "tangentPropagation" : true, "allowEdgeOverflow" : false});
        }
        {
            var Q0;
            Q0=makeQuery(id+"F29.opExtrude","CAP_FACE",FACE,{"disambiguationData":[OSD([sQuery(id+"F28.wireOp",EDGE,"E73.bottom"),sQuery(id+"F28.wireOp",EDGE,"E73.top"),sQuery(id+"F28.wireOp",EDGE,"E73.left"),sQuery(id+"F28.wireOp",EDGE,"E73.right")])],"isStart":false});
            var sketch = newSketch(context, id + "F31", { "sketchPlane" : qUnion([Q0])});
            skCircle(sketch, "E74", {"center": v(41, 15) * mm, "radius": 1 * mm});
            skCircle(sketch, "E75", {"center": v(54, 15) * mm, "radius": 1 * mm});
            skSolve(sketch);
        }
        {
            var Q0;
            Q0 = qSketchRegion(id + "F31", true);
            var Q1;
            Q1=makeQuery(id+"F31.imprint","IMPRINT",FACE,{"disambiguationData":[TD([[makeQuery(id+"F31.imprint","IMPRINT",EDGE,{"derivedFrom":sQuery(id+"F31.wireOp",EDGE,"E74")}),1.0]])]});
            extrude(context, id + "F32", {"entities" : qUnion([Q0, Q1]), "operationType" : NewBodyOperationType.REMOVE, "oppositeDirection" : true, "depth" : 7 * mm, "offsetDistance" : 25 * mm});
        }
        {
            var Q0;
            {var subQ6=sQuery(id+"F4.wireOp",EDGE,"E18.top");Q0=makeQuery(id+"F11.imprint","IMPRINT",FACE,{"disambiguationData":[TD([[makeQuery(id+"F11.imprint","IMPRINT",EDGE,{"derivedFrom":makeQuery(id+"F5.opExtrude","CAP_EDGE",EDGE,{"disambiguationData":[OSD([subQ6])],"isStart":false})}),-1.0]])]});}
            var sketch = newSketch(context, id + "F33", { "sketchPlane" : qUnion([Q0])});
            skLineSegment(sketch, "E76.bottom", {"start": v(4, 18) * mm, "end": v(23, 18) * mm});
            skLineSegment(sketch, "E76.top", {"start": v(4, 12) * mm, "end": v(23, 12) * mm});
            skLineSegment(sketch, "E76.left", {"start": v(4, 18) * mm, "end": v(4, 12) * mm});
            skLineSegment(sketch, "E76.right", {"start": v(23, 18) * mm, "end": v(23, 12) * mm});
            skSolve(sketch);
        }
        {
            var Q0;
            Q0 = qSketchRegion(id + "F33", true);
            extrude(context, id + "F34", {"entities" : qUnion([Q0]), "operationType" : NewBodyOperationType.ADD, "depth" : 5 * mm, "offsetDistance" : 25 * mm});
        }
        {
            var Q0;
            Q0=makeQuery(id+"F34.opExtrude","SWEPT_EDGE",EDGE,{"disambiguationData":[OSD([sQuery(id+"F33.wireOp",EDGE,"E76.top"),sQuery(id+"F33.wireOp",EDGE,"E76.left")])]});
            var Q1;
            Q1=makeQuery(id+"F34.opExtrude","SWEPT_EDGE",EDGE,{"disambiguationData":[OSD([sQuery(id+"F33.wireOp",EDGE,"E76.top"),sQuery(id+"F33.wireOp",EDGE,"E76.right")])]});
            fillet(context, id + "F35", {"entities" : qUnion([Q0, Q1]), "radius" : 2 * mm, "tangentPropagation" : true, "allowEdgeOverflow" : false});
        }
        {
            var Q0;
            Q0=makeQuery(id+"F34.opExtrude","CAP_FACE",FACE,{"disambiguationData":[OSD([sQuery(id+"F33.wireOp",EDGE,"E76.bottom"),sQuery(id+"F33.wireOp",EDGE,"E76.top"),sQuery(id+"F33.wireOp",EDGE,"E76.left"),sQuery(id+"F33.wireOp",EDGE,"E76.right")])],"isStart":false});
            var sketch = newSketch(context, id + "F36", { "sketchPlane" : qUnion([Q0])});
            skCircle(sketch, "E77", {"center": v(20, 15) * mm, "radius": 1 * mm});
            skCircle(sketch, "E78", {"center": v(7, 15) * mm, "radius": 1 * mm});
            skSolve(sketch);
        }
        {
            var Q0;
            Q0 = qSketchRegion(id + "F36", true);
            extrude(context, id + "F37", {"entities" : qUnion([Q0]), "operationType" : NewBodyOperationType.REMOVE, "oppositeDirection" : true, "depth" : 5 * mm, "offsetDistance" : 25 * mm});
        }
        {
            var Q0;
            Q0=makeQuery(id+"F29.boolean.opBoolean","MERGE",FACE,{"derivedFrom":[makeQuery(id+"F12.boolean.opBoolean","COPY",FACE,{"derivedFrom":makeQuery(id+"F12.opExtrude","SWEPT_FACE",FACE,{"disambiguationData":[OSD([sQuery(id+"F8.wireOp",EDGE,"E47.top")])]})}),makeQuery(id+"F29.opExtrude","CAP_FACE",FACE,{"disambiguationData":[OSD([sQuery(id+"F28.wireOp",EDGE,"E73.bottom"),sQuery(id+"F28.wireOp",EDGE,"E73.top"),sQuery(id+"F28.wireOp",EDGE,"E73.left"),sQuery(id+"F28.wireOp",EDGE,"E73.right")])],"isStart":false})]});
            var sketch = newSketch(context, id + "F38", { "sketchPlane" : qUnion([Q0])});
            skLineSegment(sketch, "E79.bottom", {"start": v(43, 17) * mm, "end": v(52, 17) * mm});
            skLineSegment(sketch, "E79.top", {"start": v(43, 16) * mm, "end": v(52, 16) * mm});
            skLineSegment(sketch, "E79.left", {"start": v(43, 17) * mm, "end": v(43, 16) * mm});
            skLineSegment(sketch, "E79.right", {"start": v(52, 17) * mm, "end": v(52, 16) * mm});
            skLineSegment(sketch, "E80.bottom", {"start": v(43, 15.5) * mm, "end": v(52, 15.5) * mm});
            skLineSegment(sketch, "E80.top", {"start": v(43, 14.5) * mm, "end": v(52, 14.5) * mm});
            skLineSegment(sketch, "E80.left", {"start": v(43, 15.5) * mm, "end": v(43, 14.5) * mm});
            skLineSegment(sketch, "E80.right", {"start": v(52, 15.5) * mm, "end": v(52, 14.5) * mm});
            skLineSegment(sketch, "E81.bottom", {"start": v(43, 14) * mm, "end": v(52, 14) * mm});
            skLineSegment(sketch, "E81.top", {"start": v(43, 13) * mm, "end": v(52, 13) * mm});
            skLineSegment(sketch, "E81.left", {"start": v(43, 14) * mm, "end": v(43, 13) * mm});
            skLineSegment(sketch, "E81.right", {"start": v(52, 14) * mm, "end": v(52, 13) * mm});
            skSolve(sketch);
        }
        {
            var Q0;
            Q0 = qSketchRegion(id + "F38", true);
            extrude(context, id + "F39", {"entities" : qUnion([Q0]), "operationType" : NewBodyOperationType.ADD, "depth" : 0.5 * mm, "offsetDistance" : 25 * mm});
        }
        {
            var Q0;
            Q0=makeQuery(id+"F39.opExtrude","CAP_EDGE",EDGE,{"disambiguationData":[OSD([sQuery(id+"F38.wireOp",EDGE,"E81.top")])],"isStart":false});
            var Q1;
            Q1=makeQuery(id+"F39.opExtrude","CAP_EDGE",EDGE,{"disambiguationData":[OSD([sQuery(id+"F38.wireOp",EDGE,"E81.bottom")])],"isStart":false});
            var Q2;
            Q2=makeQuery(id+"F39.opExtrude","CAP_EDGE",EDGE,{"disambiguationData":[OSD([sQuery(id+"F38.wireOp",EDGE,"E80.top")])],"isStart":false});
            var Q3;
            Q3=makeQuery(id+"F39.opExtrude","CAP_EDGE",EDGE,{"disambiguationData":[OSD([sQuery(id+"F38.wireOp",EDGE,"E80.bottom")])],"isStart":false});
            var Q4;
            Q4=makeQuery(id+"F39.opExtrude","CAP_EDGE",EDGE,{"disambiguationData":[OSD([sQuery(id+"F38.wireOp",EDGE,"E79.top")])],"isStart":false});
            var Q5;
            Q5=makeQuery(id+"F39.opExtrude","CAP_EDGE",EDGE,{"disambiguationData":[OSD([sQuery(id+"F38.wireOp",EDGE,"E79.bottom")])],"isStart":false});
            var Q6;
            Q6=makeQuery(id+"F39.opExtrude","CAP_EDGE",EDGE,{"disambiguationData":[OSD([sQuery(id+"F38.wireOp",EDGE,"E81.right")])],"isStart":false});
            var Q7;
            Q7=makeQuery(id+"F39.opExtrude","CAP_EDGE",EDGE,{"disambiguationData":[OSD([sQuery(id+"F38.wireOp",EDGE,"E80.right")])],"isStart":false});
            var Q8;
            Q8=makeQuery(id+"F39.opExtrude","CAP_EDGE",EDGE,{"disambiguationData":[OSD([sQuery(id+"F38.wireOp",EDGE,"E79.right")])],"isStart":false});
            var Q9;
            Q9=makeQuery(id+"F39.opExtrude","CAP_EDGE",EDGE,{"disambiguationData":[OSD([sQuery(id+"F38.wireOp",EDGE,"E79.left")])],"isStart":false});
            var Q10;
            Q10=makeQuery(id+"F39.opExtrude","CAP_EDGE",EDGE,{"disambiguationData":[OSD([sQuery(id+"F38.wireOp",EDGE,"E80.left")])],"isStart":false});
            var Q11;
            Q11=makeQuery(id+"F39.opExtrude","CAP_EDGE",EDGE,{"disambiguationData":[OSD([sQuery(id+"F38.wireOp",EDGE,"E81.left")])],"isStart":false});
            fillet(context, id + "F40", {"entities" : qUnion([Q0, Q1, Q2, Q3, Q4, Q5, Q6, Q7, Q8, Q9, Q10, Q11]), "radius" : 0.5 * mm, "tangentPropagation" : true, "allowEdgeOverflow" : false});
        }
        {
            var Q0;
            Q0=makeQuery(id+"F34.boolean.opBoolean","MERGE",FACE,{"derivedFrom":[makeQuery(id+"F12.boolean.opBoolean","COPY",FACE,{"derivedFrom":makeQuery(id+"F12.opExtrude","SWEPT_FACE",FACE,{"disambiguationData":[OSD([sQuery(id+"F8.wireOp",EDGE,"E50.top")])]})}),makeQuery(id+"F34.opExtrude","CAP_FACE",FACE,{"disambiguationData":[OSD([sQuery(id+"F33.wireOp",EDGE,"E76.bottom"),sQuery(id+"F33.wireOp",EDGE,"E76.top"),sQuery(id+"F33.wireOp",EDGE,"E76.left"),sQuery(id+"F33.wireOp",EDGE,"E76.right")])],"isStart":false})]});
            var sketch = newSketch(context, id + "F41", { "sketchPlane" : qUnion([Q0])});
            skLineSegment(sketch, "E82.bottom", {"start": v(8.95, 17) * mm, "end": v(17.95, 17) * mm});
            skLineSegment(sketch, "E82.top", {"start": v(8.95, 16) * mm, "end": v(17.95, 16) * mm});
            skLineSegment(sketch, "E82.left", {"start": v(8.95, 17) * mm, "end": v(8.95, 16) * mm});
            skLineSegment(sketch, "E82.right", {"start": v(17.95, 17) * mm, "end": v(17.95, 16) * mm});
            skLineSegment(sketch, "E83.bottom", {"start": v(8.95, 15.5) * mm, "end": v(17.95, 15.5) * mm});
            skLineSegment(sketch, "E83.top", {"start": v(8.95, 14.5) * mm, "end": v(17.95, 14.5) * mm});
            skLineSegment(sketch, "E83.left", {"start": v(8.95, 15.5) * mm, "end": v(8.95, 14.5) * mm});
            skLineSegment(sketch, "E83.right", {"start": v(17.95, 15.5) * mm, "end": v(17.95, 14.5) * mm});
            skLineSegment(sketch, "E84.bottom", {"start": v(8.95, 14) * mm, "end": v(17.95, 14) * mm});
            skLineSegment(sketch, "E84.top", {"start": v(8.95, 13) * mm, "end": v(17.95, 13) * mm});
            skLineSegment(sketch, "E84.left", {"start": v(8.95, 14) * mm, "end": v(8.95, 13) * mm});
            skLineSegment(sketch, "E84.right", {"start": v(17.95, 14) * mm, "end": v(17.95, 13) * mm});
            skSolve(sketch);
        }
        {
            var Q0;
            Q0 = qSketchRegion(id + "F41", true);
            extrude(context, id + "F42", {"entities" : qUnion([Q0]), "operationType" : NewBodyOperationType.ADD, "depth" : 0.5 * mm, "offsetDistance" : 25 * mm});
        }
        {
            var Q0;
            Q0=makeQuery(id+"F42.opExtrude","CAP_EDGE",EDGE,{"disambiguationData":[OSD([sQuery(id+"F41.wireOp",EDGE,"E84.top")])],"isStart":false});
            var Q1;
            Q1=makeQuery(id+"F42.opExtrude","CAP_EDGE",EDGE,{"disambiguationData":[OSD([sQuery(id+"F41.wireOp",EDGE,"E84.bottom")])],"isStart":false});
            var Q2;
            Q2=makeQuery(id+"F42.opExtrude","CAP_EDGE",EDGE,{"disambiguationData":[OSD([sQuery(id+"F41.wireOp",EDGE,"E83.top")])],"isStart":false});
            var Q3;
            Q3=makeQuery(id+"F42.opExtrude","CAP_EDGE",EDGE,{"disambiguationData":[OSD([sQuery(id+"F41.wireOp",EDGE,"E83.bottom")])],"isStart":false});
            var Q4;
            Q4=makeQuery(id+"F42.opExtrude","CAP_EDGE",EDGE,{"disambiguationData":[OSD([sQuery(id+"F41.wireOp",EDGE,"E82.top")])],"isStart":false});
            var Q5;
            Q5=makeQuery(id+"F42.opExtrude","CAP_EDGE",EDGE,{"disambiguationData":[OSD([sQuery(id+"F41.wireOp",EDGE,"E82.bottom")])],"isStart":false});
            var Q6;
            Q6=makeQuery(id+"F42.opExtrude","CAP_EDGE",EDGE,{"disambiguationData":[OSD([sQuery(id+"F41.wireOp",EDGE,"E83.right")])],"isStart":false});
            var Q7;
            Q7=makeQuery(id+"F42.opExtrude","CAP_EDGE",EDGE,{"disambiguationData":[OSD([sQuery(id+"F41.wireOp",EDGE,"E84.right")])],"isStart":false});
            var Q8;
            Q8=makeQuery(id+"F42.opExtrude","CAP_EDGE",EDGE,{"disambiguationData":[OSD([sQuery(id+"F41.wireOp",EDGE,"E84.left")])],"isStart":false});
            var Q9;
            Q9=makeQuery(id+"F42.opExtrude","CAP_EDGE",EDGE,{"disambiguationData":[OSD([sQuery(id+"F41.wireOp",EDGE,"E83.left")])],"isStart":false});
            var Q10;
            Q10=makeQuery(id+"F42.opExtrude","CAP_EDGE",EDGE,{"disambiguationData":[OSD([sQuery(id+"F41.wireOp",EDGE,"E82.left")])],"isStart":false});
            var Q11;
            Q11=makeQuery(id+"F42.opExtrude","CAP_EDGE",EDGE,{"disambiguationData":[OSD([sQuery(id+"F41.wireOp",EDGE,"E82.right")])],"isStart":false});
            fillet(context, id + "F43", {"entities" : qUnion([Q0, Q1, Q2, Q3, Q4, Q5, Q6, Q7, Q8, Q9, Q10, Q11]), "radius" : 0.5 * mm, "tangentPropagation" : true, "allowEdgeOverflow" : false});
        }
        {
            var Q0;
            Q0=qCreatedBy(makeId("Top.planeOp"),FACE);
            var sketch = newSketch(context, id + "F44", { "sketchPlane" : qUnion([Q0])});
            skLineSegment(sketch, "E85.bottom", {"start": v(39.49, 55.33) * mm, "end": v(58.49, 55.33) * mm});
            skLineSegment(sketch, "E85.top", {"start": v(41.49, 49.33) * mm, "end": v(56.49, 49.33) * mm});
            skLineSegment(sketch, "E85.left", {"start": v(39.49, 55.33) * mm, "end": v(39.49, 51.33) * mm});
            skLineSegment(sketch, "E85.right", {"start": v(58.49, 55.33) * mm, "end": v(58.49, 51.33) * mm});
            skPoint(sketch, "E86.visualSharp", {"position": v(58.49, 49.33) * mm});
            skArc(sketch, "E86.filletArc", {"start": v(56.49, 49.33) * mm, "mid": v(57.9, 49.92) * mm, "end": v(58.49, 51.33) * mm});
            skPoint(sketch, "E87.visualSharp", {"position": v(39.49, 49.33) * mm});
            skArc(sketch, "E87.filletArc", {"start": v(39.49, 51.33) * mm, "mid": v(40.07, 49.92) * mm, "end": v(41.49, 49.33) * mm});
            skCircle(sketch, "E88", {"center": v(55.49, 52.33) * mm, "radius": 1 * mm});
            skCircle(sketch, "E89", {"center": v(42.49, 52.33) * mm, "radius": 1 * mm});
            skSolve(sketch);
        }
        {
            var Q0;
            Q0 = qSketchRegion(id + "F44", true);
            extrude(context, id + "F45", {"entities" : qUnion([Q0]), "depth" : 2 * mm, "offsetDistance" : 25 * mm});
        }
        {
            var Q0;
            Q0=makeQuery(id+"F45.opExtrude","CAP_FACE",FACE,{"disambiguationData":[OSD([sQuery(id+"F44.wireOp",EDGE,"E85.bottom"),sQuery(id+"F44.wireOp",EDGE,"E85.top"),sQuery(id+"F44.wireOp",EDGE,"E85.left"),sQuery(id+"F44.wireOp",EDGE,"E85.right"),sQuery(id+"F44.wireOp",EDGE,"E86.filletArc"),sQuery(id+"F44.wireOp",EDGE,"E87.filletArc"),sQuery(id+"F44.wireOp",EDGE,"E88"),sQuery(id+"F44.wireOp",EDGE,"E89")])],"isStart":false});
            var sketch = newSketch(context, id + "F46", { "sketchPlane" : qUnion([Q0])});
            skCircle(sketch, "E90.0", {"center": v(55.49, 52.33) * mm, "radius": 2 * mm});
            skCircle(sketch, "E91.0", {"center": v(42.49, 52.33) * mm, "radius": 2 * mm});
            skSolve(sketch);
        }
        {
            var Q0;
            Q0 = qSketchRegion(id + "F46", true);
            extrude(context, id + "F47", {"entities" : qUnion([Q0]), "operationType" : NewBodyOperationType.REMOVE, "oppositeDirection" : true, "depth" : 0.5 * mm, "offsetDistance" : 25 * mm});
        }
        {
            var Q0;
            Q0=makeQuery(id+"F45.opExtrude","SWEPT_BODY",BODY,{"disambiguationData":[OSD([sQuery(id+"F44.wireOp",EDGE,"E85.bottom"),sQuery(id+"F44.wireOp",EDGE,"E85.top"),sQuery(id+"F44.wireOp",EDGE,"E85.left"),sQuery(id+"F44.wireOp",EDGE,"E85.right"),sQuery(id+"F44.wireOp",EDGE,"E86.filletArc"),sQuery(id+"F44.wireOp",EDGE,"E87.filletArc"),sQuery(id+"F44.wireOp",EDGE,"E88"),sQuery(id+"F44.wireOp",EDGE,"E89")])]});
            transform(context, id + "F48", {"entities" : qUnion([Q0]), "transformType" : TransformType.TRANSLATION_3D, "dx" : -36.6 * mm, "dy" : -12.9 * mm, "dz" : 40 * mm, "makeCopy" : true});
        }
        {
            var Q0;
            Q0=makeQuery(id+"F48.opPattern","COPY",BODY,{"derivedFrom":makeQuery(id+"F45.opExtrude","SWEPT_BODY",BODY,{"disambiguationData":[OSD([sQuery(id+"F44.wireOp",EDGE,"E85.bottom"),sQuery(id+"F44.wireOp",EDGE,"E85.top"),sQuery(id+"F44.wireOp",EDGE,"E85.left"),sQuery(id+"F44.wireOp",EDGE,"E85.right"),sQuery(id+"F44.wireOp",EDGE,"E86.filletArc"),sQuery(id+"F44.wireOp",EDGE,"E87.filletArc"),sQuery(id+"F44.wireOp",EDGE,"E88"),sQuery(id+"F44.wireOp",EDGE,"E89")])]}),"instanceName":"1"});
            deleteBodies(context, id + "F49", {"entities" : qUnion([Q0])});
        }
        {
            var Q0;
            Q0=makeQuery(id+"F45.opExtrude","SWEPT_BODY",BODY,{"disambiguationData":[OSD([sQuery(id+"F44.wireOp",EDGE,"E85.bottom"),sQuery(id+"F44.wireOp",EDGE,"E85.top"),sQuery(id+"F44.wireOp",EDGE,"E85.left"),sQuery(id+"F44.wireOp",EDGE,"E85.right"),sQuery(id+"F44.wireOp",EDGE,"E86.filletArc"),sQuery(id+"F44.wireOp",EDGE,"E87.filletArc"),sQuery(id+"F44.wireOp",EDGE,"E88"),sQuery(id+"F44.wireOp",EDGE,"E89")])]});
            transform(context, id + "F50", {"entities" : qUnion([Q0]), "transformType" : TransformType.TRANSLATION_3D, "dx" : -31.9 * mm, "dy" : 0 * mm, "dz" : 0 * mm, "makeCopy" : true});
        }
    });
